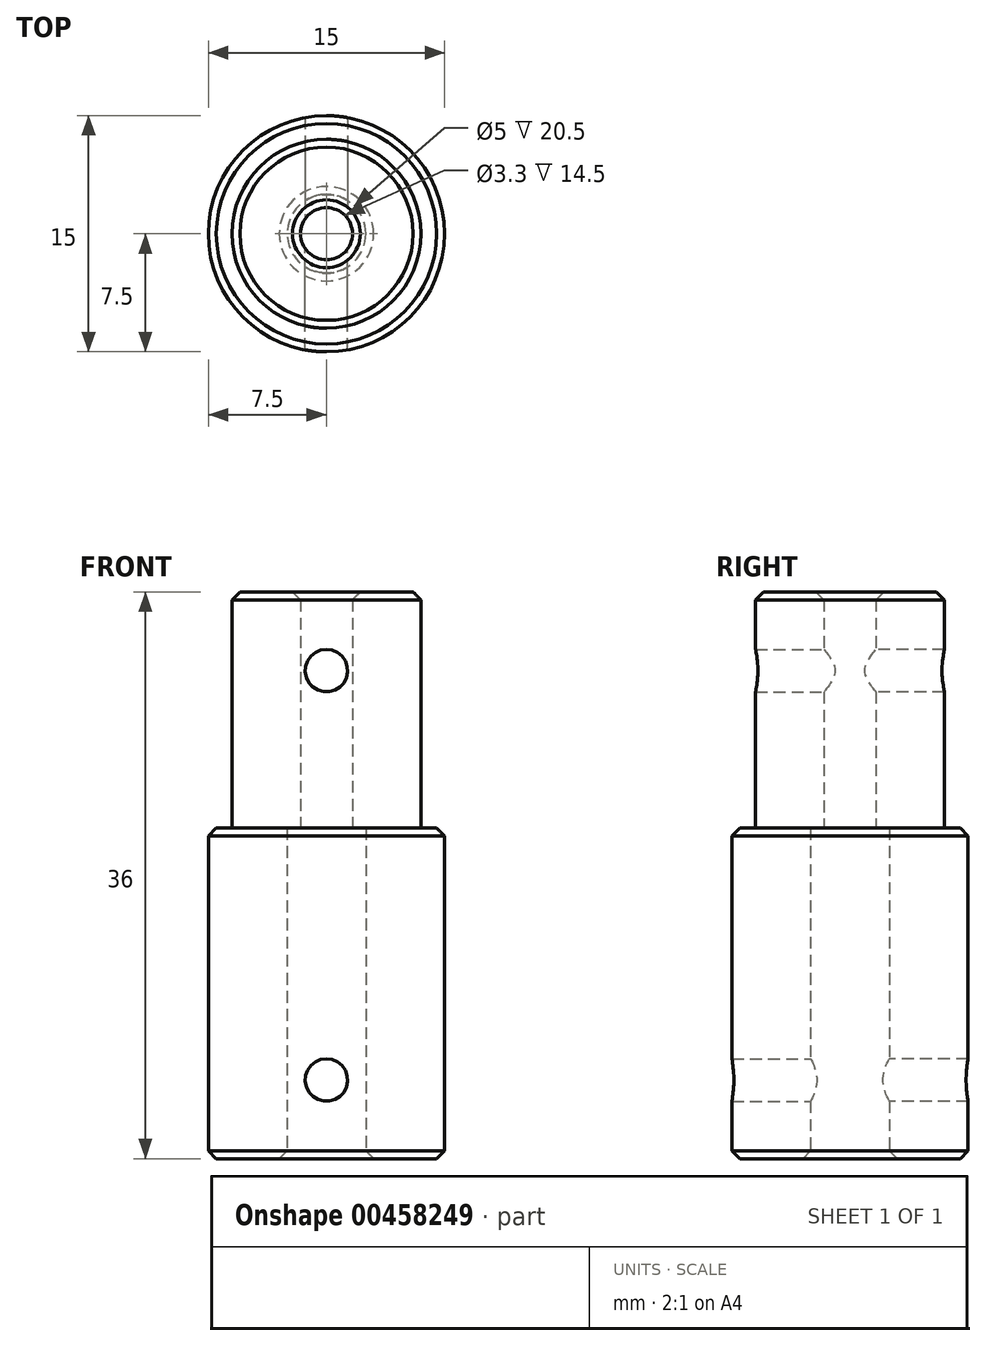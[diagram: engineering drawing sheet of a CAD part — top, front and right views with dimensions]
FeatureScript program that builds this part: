
annotation { "Feature Type Name" : "Feature", "Feature Type Description" : "" }
export const myFeature = defineFeature(function(context is Context, id is Id, definition is map)
    precondition{}
    {
        {
            var Q0;
            Q0=qCreatedBy(makeId("Top.planeOp"),FACE);
            var sketch = newSketch(context, id + "F0", { "sketchPlane" : qUnion([Q0])});
            skCircle(sketch, "E0", {"center": v(0, 0) * mm, "radius": 7.5 * mm});
            skCircle(sketch, "E1", {"center": v(0, 0) * mm, "radius": 2.5 * mm});
            skSolve(sketch);
        }
        {
            var Q0;
            Q0 = qSketchRegion(id + "F0", true);
            extrude(context, id + "F1", {"entities" : qUnion([Q0]), "depth" : 21 * mm, "offsetDistance" : 25 * mm});
        }
        {
            var Q0;
            Q0=makeQuery(id+"F1.opExtrude","CAP_FACE",FACE,{"disambiguationData":[OSD([sQuery(id+"F0.wireOp",EDGE,"E0"),sQuery(id+"F0.wireOp",EDGE,"E1")])],"isStart":false});
            var sketch = newSketch(context, id + "F2", { "sketchPlane" : qUnion([Q0])});
            skCircle(sketch, "E2", {"center": v(0, 0) * mm, "radius": 6 * mm});
            skCircle(sketch, "E3", {"center": v(0, 0) * mm, "radius": 1.65 * mm});
            skSolve(sketch);
        }
        {
            var Q0;
            Q0 = qSketchRegion(id + "F2", true);
            extrude(context, id + "F3", {"entities" : qUnion([Q0]), "operationType" : NewBodyOperationType.ADD, "depth" : 15 * mm});
        }
        {
            var Q0;
            Q0=qCreatedBy(makeId("Front.planeOp"),FACE);
            var sketch = newSketch(context, id + "F4", { "sketchPlane" : qUnion([Q0])});
            skPoint(sketch, "E4", {"position": v(0, 5) * mm});
            skPoint(sketch, "E5", {"position": v(0, 31) * mm});
            skSolve(sketch);
        }
        {
            var Q0;
            Q0=sQuery(id+"F4.wireOp",VERTEX,"E4");
            var Q1;
            Q1=sQuery(id+"F4.wireOp",VERTEX,"E5");
            var Q2;
            Q2=makeQuery(id+"F1.opExtrude","SWEPT_BODY",BODY,{"disambiguationData":[OSD([sQuery(id+"F0.wireOp",EDGE,"E0"),sQuery(id+"F0.wireOp",EDGE,"E1")])]});
            hole(context, id + "F5", {"style" : HoleStyle.SIMPLE, "endStyle" : HoleEndStyle.THROUGH, "standardTappedOrClearance" : lookupTablePath({ "standard" : "ISO", "engagement" : "50%", "pitch" : "0.5 mm", "size" : "M3", "type" : "Tapped" }), "standardBlindInLast" : lookupTablePath({ "standard" : "ISO", "engagement" : "50%", "pitch" : "0.5 mm", "size" : "M3", "type" : "Tapped" }), "holeDiameter" : 2.7 * mm, "showTappedDepth" : true, "isTappedThrough" : true, "tappedDepth" : 12 * mm, "tapClearance" : 3, "locations" : qUnion([Q0, Q1]), "scope" : qUnion([Q2]), "majorDiameter" : 3 * mm});
        }
        {
            var Q0;
            Q0=sQuery(id+"F4.wireOp",VERTEX,"E4");
            var Q1;
            Q1=sQuery(id+"F4.wireOp",VERTEX,"E5");
            var Q2;
            Q2=makeQuery(id+"F1.opExtrude","SWEPT_BODY",BODY,{"disambiguationData":[OSD([sQuery(id+"F0.wireOp",EDGE,"E0"),sQuery(id+"F0.wireOp",EDGE,"E1")])]});
            hole(context, id + "F6", {"style" : HoleStyle.SIMPLE, "endStyle" : HoleEndStyle.THROUGH, "oppositeDirection" : true, "standardTappedOrClearance" : lookupTablePath({ "standard" : "ISO", "engagement" : "50%", "pitch" : "0.5 mm", "size" : "M3", "type" : "Tapped" }), "standardBlindInLast" : lookupTablePath({ "standard" : "ISO", "engagement" : "50%", "pitch" : "0.5 mm", "size" : "M3", "type" : "Tapped" }), "holeDiameter" : 2.7 * mm, "showTappedDepth" : true, "isTappedThrough" : true, "tappedDepth" : 12 * mm, "tapClearance" : 3, "locations" : qUnion([Q0, Q1]), "scope" : qUnion([Q2]), "majorDiameter" : 3 * mm});
        }
        {
            var Q0;
            Q0=makeQuery(id+"F1.opExtrude","CAP_EDGE",EDGE,{"disambiguationData":[OSD([sQuery(id+"F0.wireOp",EDGE,"E0")])],"isStart":true});
            var Q1;
            Q1=makeQuery(id+"F1.opExtrude","CAP_EDGE",EDGE,{"disambiguationData":[OSD([sQuery(id+"F0.wireOp",EDGE,"E0")])],"isStart":false});
            var Q2;
            Q2=makeQuery(id+"F3.opExtrude","CAP_EDGE",EDGE,{"disambiguationData":[OSD([sQuery(id+"F2.wireOp",EDGE,"E2")])],"isStart":false});
            var Q3;
            Q3=makeQuery(id+"F1.opExtrude","CAP_EDGE",EDGE,{"disambiguationData":[OSD([sQuery(id+"F0.wireOp",EDGE,"E1")])],"isStart":true});
            var Q4;
            Q4=makeQuery(id+"F3.opExtrude","CAP_EDGE",EDGE,{"disambiguationData":[OSD([sQuery(id+"F2.wireOp",EDGE,"E2")])],"isStart":true});
            var Q5;
            Q5=makeQuery(id+"F1.opExtrude","CAP_EDGE",EDGE,{"disambiguationData":[OSD([sQuery(id+"F0.wireOp",EDGE,"E1")])],"isStart":false});
            var Q6;
            Q6=makeQuery(id+"F3.opExtrude","CAP_EDGE",EDGE,{"disambiguationData":[OSD([sQuery(id+"F2.wireOp",EDGE,"E3")])],"isStart":false});
            chamfer(context, id + "F7", {"entities" : qUnion([Q0, Q1, Q2, Q3, Q4, Q5, Q6]), "width" : .5 * mm, "tangentPropagation" : true});
        }
    });
